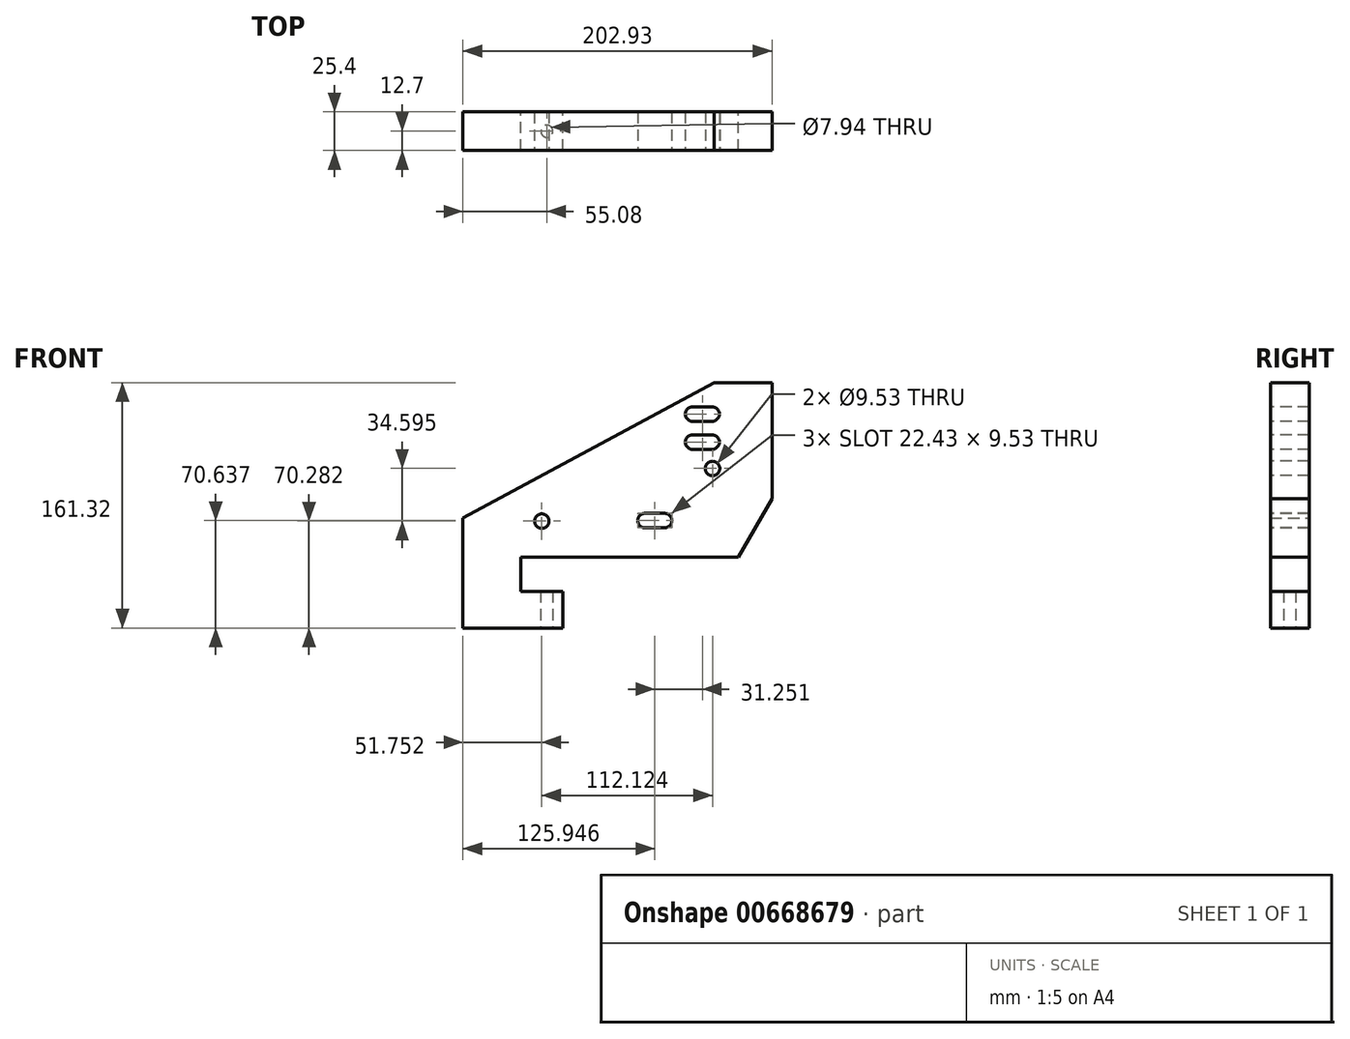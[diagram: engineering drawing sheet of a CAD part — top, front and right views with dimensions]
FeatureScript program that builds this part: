
annotation { "Feature Type Name" : "Feature", "Feature Type Description" : "" }
export const myFeature = defineFeature(function(context is Context, id is Id, definition is map)
    precondition{}
    {
        {
            var Q0;
            Q0=qCreatedBy(makeId("Front.planeOp"),FACE);
            var sketch = newSketch(context, id + "F0", { "sketchPlane" : qUnion([Q0])});
            skLineSegment(sketch, "E0", {"start": v(0, 0) * mm, "end": v(0, 72.31) * mm});
            skLineSegment(sketch, "E1", {"start": v(0, 72.31) * mm, "end": v(164.83, 161.32) * mm});
            skLineSegment(sketch, "E2", {"start": v(164.83, 161.32) * mm, "end": v(202.93, 161.32) * mm});
            skLineSegment(sketch, "E3", {"start": v(202.93, 161.32) * mm, "end": v(202.93, 85.12) * mm});
            skLineSegment(sketch, "E4", {"start": v(180.98, 46.47) * mm, "end": v(202.93, 85.12) * mm});
            skLineSegment(sketch, "E5", {"start": v(180.98, 46.47) * mm, "end": v(38.1, 46.47) * mm});
            skLineSegment(sketch, "E6", {"start": v(38.1, 46.47) * mm, "end": v(38.1, 24.16) * mm});
            skLineSegment(sketch, "E7", {"start": v(38.1, 24.16) * mm, "end": v(65.58, 24.16) * mm});
            skLineSegment(sketch, "E8", {"start": v(65.58, 24.16) * mm, "end": v(65.58, 0) * mm});
            skLineSegment(sketch, "E9", {"start": v(65.58, 0) * mm, "end": v(0, 0) * mm});
            skSolve(sketch);
        }
        {
            var Q0;
            Q0 = qSketchRegion(id + "F0", true);
            extrude(context, id + "F1", {"entities" : qUnion([Q0]), "depth" : 25.4 * mm, "offsetDistance" : 25.4 * mm});
        }
        {
            var Q0;
            Q0=makeQuery(id+"F1.opExtrude","CAP_FACE",FACE,{"disambiguationData":[OSD([sQuery(id+"F0.wireOp",EDGE,"E0"),sQuery(id+"F0.wireOp",EDGE,"E1"),sQuery(id+"F0.wireOp",EDGE,"E2"),sQuery(id+"F0.wireOp",EDGE,"E3"),sQuery(id+"F0.wireOp",EDGE,"E4"),sQuery(id+"F0.wireOp",EDGE,"E5"),sQuery(id+"F0.wireOp",EDGE,"E6"),sQuery(id+"F0.wireOp",EDGE,"E7"),sQuery(id+"F0.wireOp",EDGE,"E8"),sQuery(id+"F0.wireOp",EDGE,"E9")])],"isStart":false});
            var sketch = newSketch(context, id + "F2", { "sketchPlane" : qUnion([Q0])});
            skCircle(sketch, "E10", {"center": v(51.75, 70.28) * mm, "radius": 4.76 * mm});
            skCircle(sketch, "E11", {"center": v(163.88, 104.88) * mm, "radius": 4.76 * mm});
            skLineSegment(sketch, "E12", {"start": v(114.73, 70.64) * mm, "end": v(137.16, 70.64) * mm, "construction": true});
            skLineSegment(sketch, "E13", {"start": v(125.95, 75.4) * mm, "end": v(125.95, 65.87) * mm, "construction": true});
            skPoint(sketch, "E13.startSnap0", {"position": v(125.95, 70.64) * mm});
            skLineSegment(sketch, "E14", {"start": v(119.5, 75.4) * mm, "end": v(132.4, 75.4) * mm});
            skLineSegment(sketch, "E15", {"start": v(119.5, 65.87) * mm, "end": v(132.4, 65.87) * mm});
            skArc(sketch, "E16", {"start": v(119.5, 75.4) * mm, "mid": v(114.73, 70.64) * mm, "end": v(119.5, 65.87) * mm});
            skArc(sketch, "E17", {"start": v(132.4, 65.87) * mm, "mid": v(137.16, 70.64) * mm, "end": v(132.4, 75.4) * mm});
            skLineSegment(sketch, "E18", {"start": v(150.75, 145.38) * mm, "end": v(163.65, 145.38) * mm});
            skLineSegment(sketch, "E19", {"start": v(150.75, 135.85) * mm, "end": v(163.65, 135.85) * mm});
            skArc(sketch, "E20", {"start": v(150.75, 145.38) * mm, "mid": v(145.98, 140.61) * mm, "end": v(150.75, 135.85) * mm});
            skArc(sketch, "E21", {"start": v(163.65, 135.85) * mm, "mid": v(168.41, 140.61) * mm, "end": v(163.65, 145.38) * mm});
            skLineSegment(sketch, "E22", {"start": v(150.75, 126.96) * mm, "end": v(163.65, 126.96) * mm});
            skLineSegment(sketch, "E23", {"start": v(150.75, 117.44) * mm, "end": v(163.65, 117.44) * mm});
            skArc(sketch, "E24", {"start": v(150.75, 126.96) * mm, "mid": v(145.98, 122.2) * mm, "end": v(150.75, 117.44) * mm});
            skArc(sketch, "E25", {"start": v(163.65, 117.44) * mm, "mid": v(168.41, 122.2) * mm, "end": v(163.65, 126.96) * mm});
            skSolve(sketch);
        }
        {
            var Q0;
            Q0 = qSketchRegion(id + "F2", true);
            extrude(context, id + "F3", {"entities" : qUnion([Q0]), "operationType" : NewBodyOperationType.REMOVE, "endBound" : BoundingType.THROUGH_ALL, "oppositeDirection" : true, "depth" : 25.4 * mm, "offsetDistance" : 25.4 * mm});
        }
        {
            var Q0;
            Q0=makeQuery(id+"F1.opExtrude","SWEPT_FACE",FACE,{"disambiguationData":[OSD([sQuery(id+"F0.wireOp",EDGE,"E9")])]});
            var sketch = newSketch(context, id + "F4", { "sketchPlane" : qUnion([Q0])});
            skPoint(sketch, "E26", {"position": v(55.08, 12.7) * mm});
            skPoint(sketch, "E26.positionSnap0", {"position": v(65.58, 12.7) * mm});
            skSolve(sketch);
        }
        {
            var Q0;
            Q0=sQuery(id+"F4.wireOp",VERTEX,"E26");
            var Q1;
            Q1=makeQuery(id+"F1.opExtrude","SWEPT_BODY",BODY,{"disambiguationData":[OSD([sQuery(id+"F0.wireOp",EDGE,"E0"),sQuery(id+"F0.wireOp",EDGE,"E1"),sQuery(id+"F0.wireOp",EDGE,"E2"),sQuery(id+"F0.wireOp",EDGE,"E3"),sQuery(id+"F0.wireOp",EDGE,"E4"),sQuery(id+"F0.wireOp",EDGE,"E5"),sQuery(id+"F0.wireOp",EDGE,"E6"),sQuery(id+"F0.wireOp",EDGE,"E7"),sQuery(id+"F0.wireOp",EDGE,"E8"),sQuery(id+"F0.wireOp",EDGE,"E9")])]});
            hole(context, id + "F5", {"style" : HoleStyle.SIMPLE, "endStyle" : HoleEndStyle.BLIND, "standardTappedOrClearance" : lookupTablePath({ "standard" : "ANSI", "engagement" : "75%", "pitch" : "16 tpi", "size" : "3/8", "type" : "Tapped" }), "standardBlindInLast" : lookupTablePath({ "standard" : "ANSI", "fit" : "Normal", "engagement" : "75%", "pitch" : "16 tpi", "size" : "3/8", "type" : "Clearance & tapped" }), "holeDiameter" : 7.94 * mm, "majorDiameter" : 9.52 * mm, "showTappedDepth" : true, "holeDepth" : 25.4 * mm, "isTappedThrough" : true, "tappedDepth" : 20.64 * mm, "tapClearance" : 3, "startFromSketch" : true, "locations" : qUnion([Q0]), "scope" : qUnion([Q1])});
        }
    });
